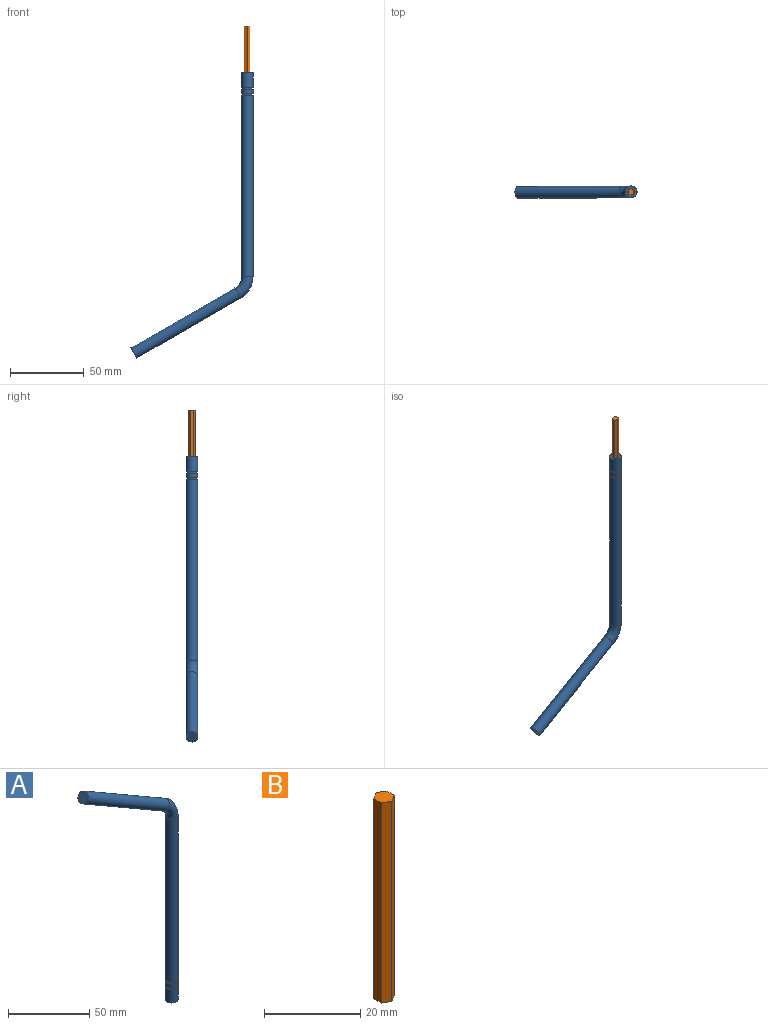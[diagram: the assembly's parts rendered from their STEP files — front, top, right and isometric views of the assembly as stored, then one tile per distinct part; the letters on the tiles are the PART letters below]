
ASSEMBLY  parts=2 mates=1
PART A: 15 faces, bbox 84.3x7.9x193.9 mm
  f0: plane 7.94x7.94mm, normal (0,0,-1), area 34mm2, adj f1,f2
  f1: cylinder r=3.97mm len=10.1mm, axis (0,0,1), area 251.8mm2, adj f0,f5
  f2: cylinder r=2.22mm len=19.05mm, axis (0,0,-1), area 266mm2, adj f0,f3
  f3: plane 4.45x4.45mm, normal (0,0,-1), area 15.5mm2, adj f2
  f4: cylinder r=3.33mm len=6.67mm, axis (0,0,1), area 21.3mm2, adj f5,f6
  f5: plane 7.94x7.94mm, normal (0,0,1), area 14.6mm2, adj f1,f4
  f6: plane 7.94x7.94mm, normal (0,0,-1), area 14.6mm2, adj f4,f7
  f7: cylinder r=3.97mm len=7.94mm, axis (0,0,1), area 79.2mm2, adj f6,f9
  f8: cylinder r=3.33mm len=6.67mm, axis (0,0,1), area 21.3mm2, adj f9,f10
  f9: plane 7.94x7.94mm, normal (0,0,1), area 14.6mm2, adj f7,f8
  f10: plane 7.94x7.94mm, normal (0,0,-1), area 14.6mm2, adj f8,f14
  f11: plane 7.94x6.87mm, normal (-0.87,0,0.5), area 49.5mm2, adj f12
  f12: cylinder r=3.97mm len=74.61mm, axis (-0.87,0,0.5), area 2034mm2, adj f11,f13
  f13: torus R=12.7mm, axis (0,-1,0), area 331.6mm2, adj f12,f14
  f14: cylinder r=3.97mm len=123.41mm, axis (0,0,1), area 3077.5mm2, adj f10,f13
PART B: 8 faces, bbox 3.8x4.4x50.8 mm
  f0: plane 50.8x1.92mm, normal (-0.5,-0.87,0), area 112.9mm2, adj f1,f5,f6,f7
  f1: plane 50.8x2.22mm, normal (-1,0,0), area 112.9mm2, adj f0,f2,f6,f7
  f2: plane 50.8x1.92mm, normal (-0.5,0.87,0), area 112.9mm2, adj f1,f3,f6,f7
  f3: plane 50.8x1.92mm, normal (0.5,0.87,0), area 112.9mm2, adj f2,f4,f6,f7
  f4: plane 50.8x2.22mm, normal (1,0,0), area 112.9mm2, adj f3,f5,f6,f7
  f5: plane 50.8x1.92mm, normal (0.5,-0.87,0), area 112.9mm2, adj f0,f4,f6,f7
  f6: plane 4.45x3.85mm, normal (0,0,-1), area 12.8mm2, adj f0,f1,f2,f3,f4,f5
  f7: plane 4.45x3.85mm, normal (0,0,1), area 12.8mm2, adj f0,f1,f2,f3,f4,f5
PLACE A rot(axis=(1,0,0),180deg) t=(-113.8,-3.63,1.17)mm fixed
PLACE B t=(-113.8,-3.63,13.87)mm
MATE fastened A.f2 <-> B.f6  axis (0,0,1) through (-113.8,-3.63,-17.88)mm
